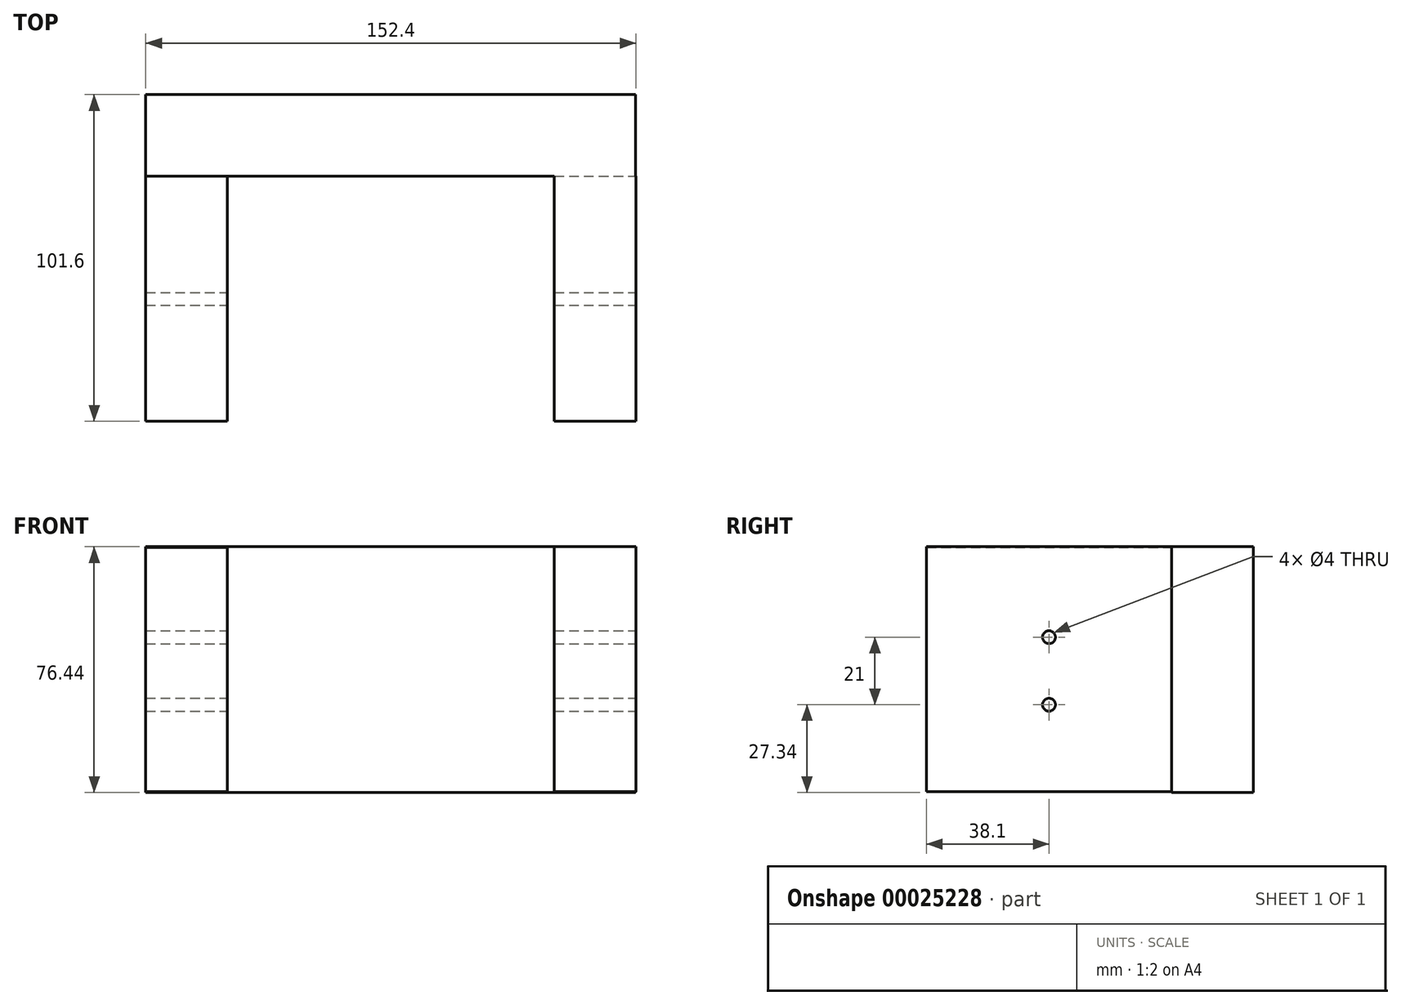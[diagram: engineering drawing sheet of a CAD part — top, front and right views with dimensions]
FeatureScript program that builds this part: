
annotation { "Feature Type Name" : "Feature", "Feature Type Description" : "" }
export const myFeature = defineFeature(function(context is Context, id is Id, definition is map)
    precondition{}
    {
        {
            var Q0;
            Q0=qCreatedBy(makeId("Front.planeOp"),FACE);
            var sketch = newSketch(context, id + "F0", { "sketchPlane" : qUnion([Q0])});
            skLineSegment(sketch, "E0.bottom", {"start": v(0, 0) * mm, "end": v(152.4, 0) * mm});
            skLineSegment(sketch, "E0.top", {"start": v(0, -76.2) * mm, "end": v(152.4, -76.2) * mm});
            skLineSegment(sketch, "E0.left", {"start": v(0, 0) * mm, "end": v(0, -76.2) * mm});
            skLineSegment(sketch, "E0.right", {"start": v(152.4, 0) * mm, "end": v(152.4, -76.2) * mm});
            skLineSegment(sketch, "E1", {"start": v(0, -0.15) * mm, "end": v(25.4, -0.15) * mm});
            skLineSegment(sketch, "E2", {"start": v(152.4, 0.15) * mm, "end": v(127, 0.15) * mm});
            skLineSegment(sketch, "E3", {"start": v(25.4, -0.15) * mm, "end": v(25.4, -76.2) * mm});
            skLineSegment(sketch, "E4", {"start": v(25.4, -76.2) * mm, "end": v(0, -76.2) * mm});
            skLineSegment(sketch, "E5", {"start": v(127, 0.15) * mm, "end": v(127, -76.2) * mm});
            skLineSegment(sketch, "E6", {"start": v(127, -76.2) * mm, "end": v(152.4, -76.2) * mm});
            skSolve(sketch);
        }
        {
            var Q0;
            {var subQ1=sQuery(id+"F0.wireOp",EDGE,"E1");Q0=makeQuery(id+"F0.imprint","IMPRINT",FACE,{"disambiguationData":[TD([[makeQuery(id+"F0.imprint","IMPRINT",EDGE,{"derivedFrom":subQ1}),-1.0]])]});}
            var Q1;
            {var subQ4=sQuery(id+"F0.wireOp",EDGE,"E0.right");Q1=makeQuery(id+"F0.imprint","IMPRINT",FACE,{"disambiguationData":[TD([[makeQuery(id+"F0.imprint","IMPRINT",EDGE,{"derivedFrom":subQ4}),-1.0]])]});}
            extrude(context, id + "F1", {"entities" : qUnion([Q0, Q1]), "depth" : 76.2 * mm});
        }
        {
            var Q0;
            {var subQ1=sQuery(id+"F0.wireOp",EDGE,"E1");Q0=makeQuery(id+"F0.imprint","IMPRINT",FACE,{"disambiguationData":[TD([[makeQuery(id+"F0.imprint","IMPRINT",EDGE,{"derivedFrom":subQ1}),-1.0]])]});}
            var sketch = newSketch(context, id + "F2", { "sketchPlane" : qUnion([Q0])});
            skLineSegment(sketch, "E7.bottom", {"start": v(152.2, 0) * mm, "end": v(0, 0) * mm});
            skLineSegment(sketch, "E7.top", {"start": v(152.2, -76.44) * mm, "end": v(0, -76.44) * mm});
            skLineSegment(sketch, "E7.left", {"start": v(152.2, 0) * mm, "end": v(152.2, -76.44) * mm});
            skLineSegment(sketch, "E7.right", {"start": v(0, 0) * mm, "end": v(0, -76.44) * mm});
            skSolve(sketch);
        }
        {
            var Q0;
            {var subQ3=sQuery(id+"F2.wireOp",EDGE,"E7.bottom");Q0=makeQuery(id+"F2.imprint","IMPRINT",FACE,{"disambiguationData":[TD([[makeQuery(id+"F2.imprint","IMPRINT",EDGE,{"derivedFrom":subQ3}),1.0]])]});}
            extrude(context, id + "F3", {"entities" : qUnion([Q0]), "operationType" : NewBodyOperationType.ADD, "oppositeDirection" : true, "depth" : 25.4 * mm});
        }
        {
            var Q0;
            {var subQ1=sQuery(id+"F0.wireOp",EDGE,"E1");Q0=makeQuery(id+"F0.imprint","IMPRINT",FACE,{"disambiguationData":[TD([[makeQuery(id+"F0.imprint","IMPRINT",EDGE,{"derivedFrom":subQ1}),-1.0]])]});}
            extrude(context, id + "F4", {"entities" : qUnion([Q0]), "operationType" : NewBodyOperationType.ADD, "oppositeDirection" : true, "depth" : 25.4 * mm});
        }
        {
            var Q0;
            Q0=makeQuery(id+"F1.opExtrude","SWEPT_FACE",FACE,{"disambiguationData":[OSD([sQuery(id+"F0.wireOp",EDGE,"E0.right")])]});
            var sketch = newSketch(context, id + "F5", { "sketchPlane" : qUnion([Q0])});
            skCircle(sketch, "E8", {"center": v(-38.1, -28.1) * mm, "radius": 2 * mm});
            skCircle(sketch, "E9", {"center": v(-38.1, -49.1) * mm, "radius": 2 * mm});
            skSolve(sketch);
        }
        {
            var Q0;
            Q0=makeQuery(id+"F5.imprint","IMPRINT",FACE,{"disambiguationData":[TD([[makeQuery(id+"F5.imprint","IMPRINT",EDGE,{"derivedFrom":sQuery(id+"F5.wireOp",EDGE,"E8")}),1.0]])]});
            var Q1;
            Q1=makeQuery(id+"F5.imprint","IMPRINT",FACE,{"disambiguationData":[TD([[makeQuery(id+"F5.imprint","IMPRINT",EDGE,{"derivedFrom":sQuery(id+"F5.wireOp",EDGE,"E9")}),1.0]])]});
            extrude(context, id + "F6", {"entities" : qUnion([Q0, Q1]), "operationType" : NewBodyOperationType.REMOVE, "endBound" : BoundingType.THROUGH_ALL, "oppositeDirection" : true, "depth" : 25.4 * mm});
        }
    });
